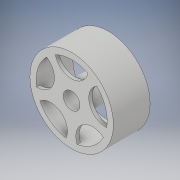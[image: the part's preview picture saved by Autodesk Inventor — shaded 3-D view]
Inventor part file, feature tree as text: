
AUTODESK INVENTOR PART (.ipt)
format: ipt  version: 2019 (Build 230136000, 136)  size: 150,016 bytes
history: native  units: mm
features: extrude x3, sketch x3, projected_geometry x3, pattern_circular x1
ambient origin geometry x8: Origin, YZ Plane, XZ Plane, XY Plane, X Axis, Y Axis, Z Axis, Center Point
bodies: Solid1 (feature_tree)
feature tree (10):
  extrude  "Extrusion1"  Depth=10.0mm
  extrude  "Extrusion2"  Depth=2.0mm TaperAngle=0.0deg
  extrude  "Extrusion3"  Depth=2.0mm TaperAngle=0.0deg
  pattern_circular  "Circular Pattern1"  Count=5 Angle=360.0deg
  sketch  "Sketch1"  dims[d0=50.0mm d1=10.0mm]
  sketch  "Sketch2"  dims[d2=20.0mm d3=0.0mm d4=2.0mm d5=0.0mm]
  projected_geometry  "Projected Loop1"
  projected_geometry  "Projected Loop2"
  projected_geometry  "Projected Loop3"
  sketch  "Sketch3"  dims[d6=20.0mm d7=2.0mm d8=0.0mm d9=50.0mm d10=360.0deg]
